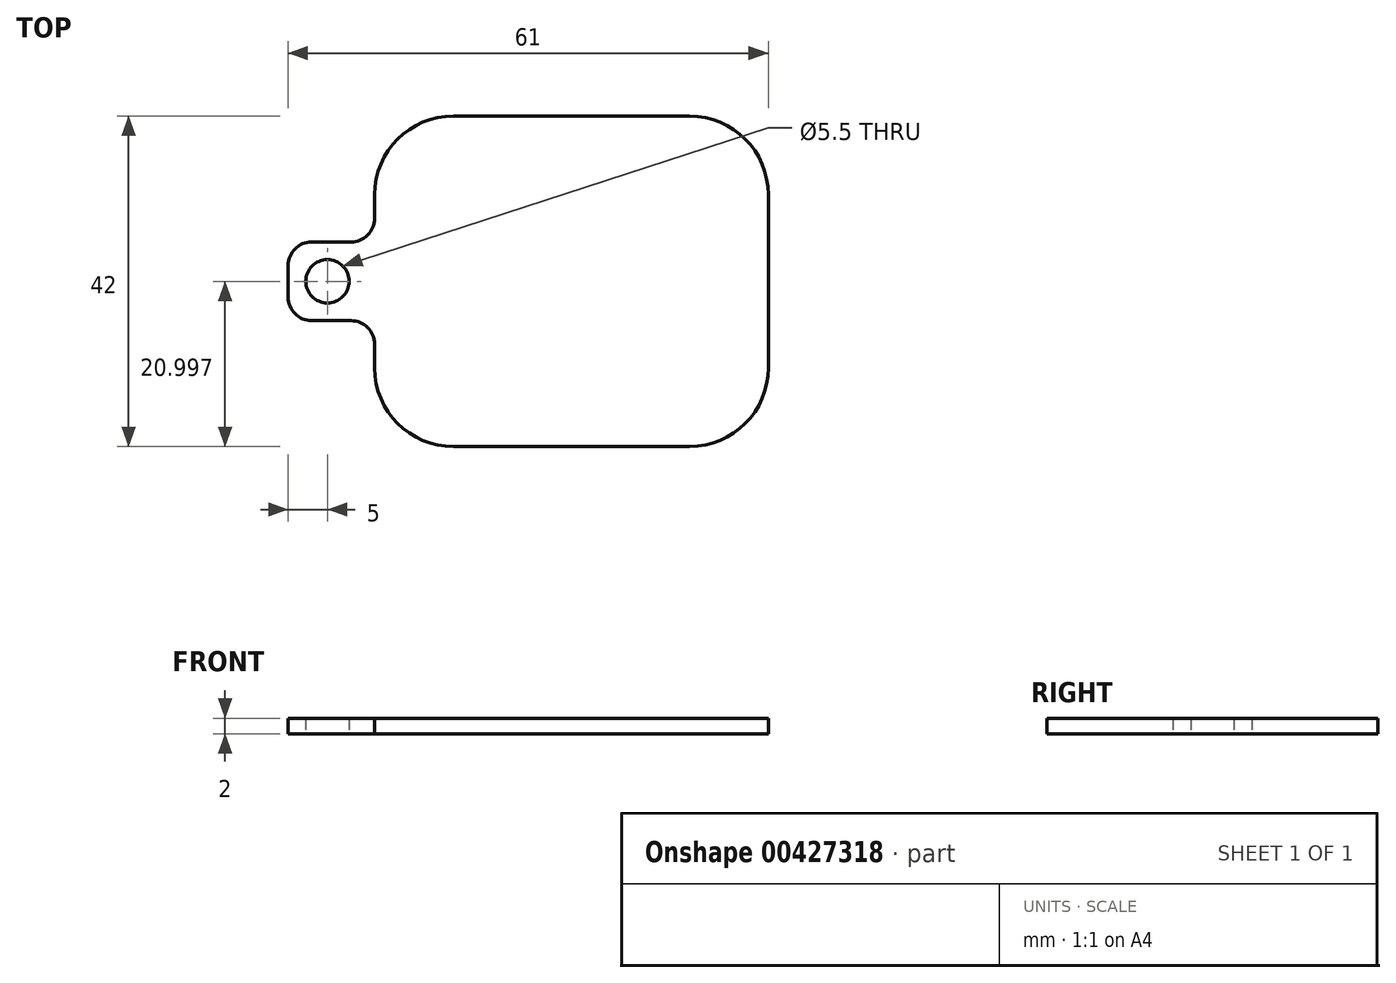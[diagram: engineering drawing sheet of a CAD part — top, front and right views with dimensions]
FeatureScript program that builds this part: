
annotation { "Feature Type Name" : "Feature", "Feature Type Description" : "" }
export const myFeature = defineFeature(function(context is Context, id is Id, definition is map)
    precondition{}
    {
        {
            var Q0;
            Q0=qCreatedBy(makeId("Top.planeOp"),FACE);
            var sketch = newSketch(context, id + "F0", { "sketchPlane" : qUnion([Q0])});
            skLineSegment(sketch, "E0.bottom", {"start": v(-33.35, -26.02) * mm, "end": v(-63.35, -26.02) * mm});
            skLineSegment(sketch, "E0.top", {"start": v(-33.35, -68.02) * mm, "end": v(-63.35, -68.02) * mm});
            skLineSegment(sketch, "E0.left", {"start": v(-23.35, -36.02) * mm, "end": v(-23.35, -58.02) * mm});
            skLineSegment(sketch, "E0.right", {"start": v(-73.35, -36.02) * mm, "end": v(-73.35, -39.02) * mm});
            skLineSegment(sketch, "E1.bottom", {"start": v(-81.35, -42.02) * mm, "end": v(-76.35, -42.02) * mm});
            skLineSegment(sketch, "E1.top", {"start": v(-81.35, -52.02) * mm, "end": v(-76.35, -52.02) * mm});
            skLineSegment(sketch, "E1.left", {"start": v(-84.35, -45.02) * mm, "end": v(-84.35, -49.02) * mm});
            skLineSegment(sketch, "E2.trimOffspring", {"start": v(-73.35, -55.02) * mm, "end": v(-73.35, -58.02) * mm});
            skPoint(sketch, "E3.visualSharp", {"position": v(-73.35, -42.02) * mm});
            skArc(sketch, "E3.filletArc", {"start": v(-76.35, -42.02) * mm, "mid": v(-74.23, -41.14) * mm, "end": v(-73.35, -39.02) * mm});
            skPoint(sketch, "E4.visualSharp", {"position": v(-84.35, -42.02) * mm});
            skArc(sketch, "E4.filletArc", {"start": v(-81.35, -42.02) * mm, "mid": v(-83.47, -42.9) * mm, "end": v(-84.35, -45.02) * mm});
            skPoint(sketch, "E5.visualSharp", {"position": v(-84.35, -52.02) * mm});
            skArc(sketch, "E5.filletArc", {"start": v(-84.35, -49.02) * mm, "mid": v(-83.47, -51.14) * mm, "end": v(-81.35, -52.02) * mm});
            skPoint(sketch, "E6.visualSharp", {"position": v(-73.35, -52.02) * mm});
            skArc(sketch, "E6.filletArc", {"start": v(-73.35, -55.02) * mm, "mid": v(-74.23, -52.9) * mm, "end": v(-76.35, -52.02) * mm});
            skPoint(sketch, "E7.visualSharp", {"position": v(-73.35, -26.02) * mm});
            skArc(sketch, "E7.filletArc", {"start": v(-63.35, -26.02) * mm, "mid": v(-70.42, -28.95) * mm, "end": v(-73.35, -36.02) * mm});
            skPoint(sketch, "E8.visualSharp", {"position": v(-73.35, -68.02) * mm});
            skArc(sketch, "E8.filletArc", {"start": v(-73.35, -58.02) * mm, "mid": v(-70.42, -65.1) * mm, "end": v(-63.35, -68.02) * mm});
            skPoint(sketch, "E9.visualSharp", {"position": v(-23.35, -26.02) * mm});
            skArc(sketch, "E9.filletArc", {"start": v(-23.35, -36.02) * mm, "mid": v(-26.28, -28.95) * mm, "end": v(-33.35, -26.02) * mm});
            skPoint(sketch, "E10.visualSharp", {"position": v(-23.35, -68.02) * mm});
            skArc(sketch, "E10.filletArc", {"start": v(-33.35, -68.02) * mm, "mid": v(-26.28, -65.1) * mm, "end": v(-23.35, -58.02) * mm});
            skCircle(sketch, "E11", {"center": v(-79.35, -47.02) * mm, "radius": 2.75 * mm});
            skPoint(sketch, "E11.centerSnap0", {"position": v(-84.35, -47.02) * mm});
            skSolve(sketch);
        }
        {
            var Q0;
            Q0=makeQuery(id+"F0.imprint","IMPRINT",FACE,{"disambiguationData":[TD([[makeQuery(id+"F0.imprint","IMPRINT",EDGE,{"derivedFrom":sQuery(id+"F0.wireOp",EDGE,"E0.bottom")}),1.0]])]});
            extrude(context, id + "F1", {"entities" : qUnion([Q0]), "depth" : 2 * mm});
        }
    });
